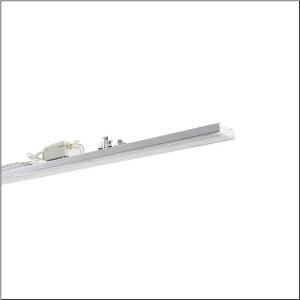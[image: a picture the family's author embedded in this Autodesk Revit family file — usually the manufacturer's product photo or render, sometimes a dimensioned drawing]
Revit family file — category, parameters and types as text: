
# Revit family: licross_21_recessed_ho_52te12mn4fxm
name_source: partatom
category: Lighting Fixtures
units: mm (PartAtom-declared; Revit-internal decimal feet)

## family parameters
Cut with Voids When Loaded = No
Host = Face
Light Source = No
Part Type = Normal
Room Calculation Point = No
Round Connector Dimension = Use Diameter
Shared = No

## types (1)
- --- (1 x LED, 15100 lm, 83.1 W, 4000K)
    Apparent Load = 83 VA
    CIE Flux Codes = 69 91 98 100 100
    Color Rendering = 80
    Color Temperature = 4000K
    Default Elevation = 1800 mm
    Description = Licross 21 Recessed HO, luminaire insert, of sheet steel, galvanised, coil coated, white, length: 1.500mm, width: 66mm, height: 67mm, LED rated luminous flux: 15.100lm, light colour: 840, SDCM (Standard Deviation of Colour Matching)MacAdam ≤ 3 SDCM (initial), control gear: ON/OFF Multilumen, with plug, 3-pole, with phase selection, mains connection: 220..240V, AC, 50/60Hz, rated input power: 83W, internal wiring halogen-free, primary optical cover: cover, of PMMA, light emission: direct distribution, primary light characteristic: symmetric, protection rating (complete): IP54, insulation class (complete): insulation class I (protective earthing), certification: CE, ENEC, VDE, UKCA, protection symbol: D if used in an environment with non-conductive dust loads with corresponding accessories, impact resistance: IK06, permissible ambient temperature for indoor applications: -35..+30°C, corresponds to IFS (International Featured Standards) requirements for safety and quality in the food industry, reducing of maximum allowable ambient temperature of 5°C with ceiling mounting, LABS conformity tested according to VDMA 24364:2018-05, The light source and the operating device comply with the requirements of the Ecodesign Regulation (EU) 2019/2020 and are replaceable in accordance with this regulation, packaging unit: 1 piece
    Height = 58 mm
    Lamp = 1 x LED
    Lamp Light Flux = 15100 lm
    Lamp Power = 83.1 W
    Lamp count = 1
    Length = 1500 mm
    Luminous efficacy = 182 lm/W
    Manufacturer = Siteco
    ModVariant = No
    Model = 52TE12MN4FXM
    Mounting Place = Ceiling
    Mounting Type = Pendant
    Number of Poles = 1
    OnlyDefault = Yes
    Power Factor = 1
    Product Name = Licross 21 Recessed HO
    Product group = luminaire insert | ceiling pendant
    ProductGroupID = 901
    Protection Class = Protection class I
    Protection Degree = IP 54
    RLX_Detail_Level = 1
    RLX_Emergency_Light_Flux = 0 lm
    RLX_Emergency_Type = 0
    RLX_Emergency_Type_DB = No
    RlxData = <blob elided: 22609 chars, md5=30b73d9e>
    Socket = socket
    Standby Power = 0 W
    System Light Flux = 15100 lm
    System Power = 83 W
    Type Comments = factory setting: luminous flux: 100 % | (A | C | E) | 195 mA
    Type Image = l_1296930.jpg
    URL = http://relux.com
    VarID = @adj_104613
    Voltage = 0 V
    Weight = 0.00 kg
    Width = 66 mm

## geometry (parser evidence)
native form markers: Blend x4, Sweep x12
no freeform markers — native parametric forms only
